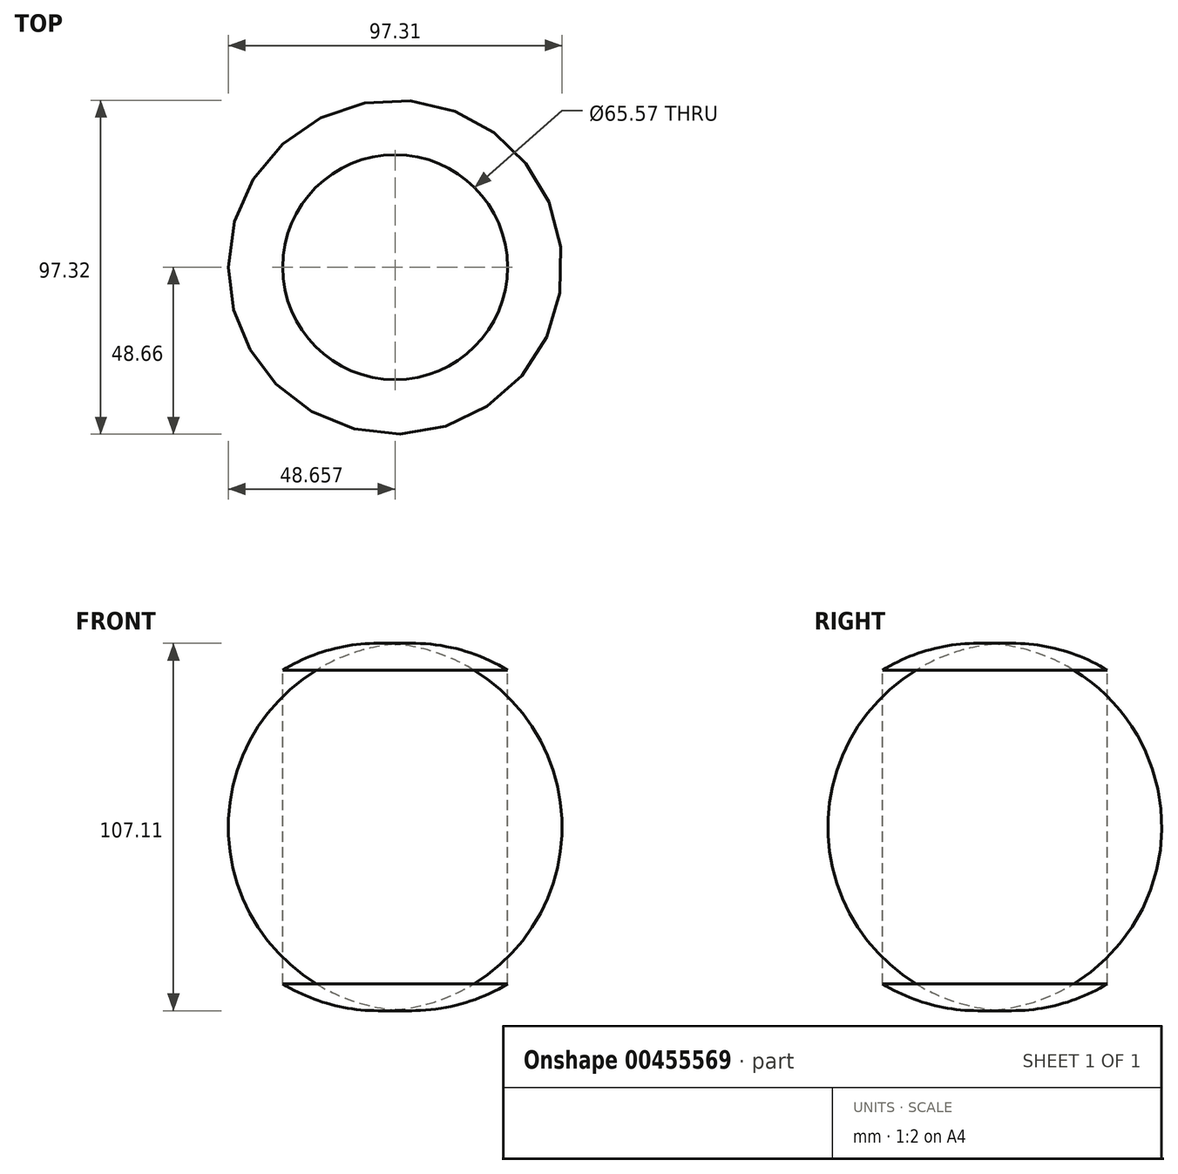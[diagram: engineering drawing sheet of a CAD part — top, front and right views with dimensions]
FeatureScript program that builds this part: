
annotation { "Feature Type Name" : "Feature", "Feature Type Description" : "" }
export const myFeature = defineFeature(function(context is Context, id is Id, definition is map)
    precondition{}
    {
        {
            var Q0;
            Q0=qCreatedBy(makeId("Top.planeOp"),FACE);
            var sketch = newSketch(context, id + "F0", { "sketchPlane" : qUnion([Q0])});
            skLineSegment(sketch, "E0", {"start": v(-39.7, 55.95) * mm, "end": v(-39.7, -36.1) * mm});
            skLineSegment(sketch, "E1", {"start": v(-13.54, 56.25) * mm, "end": v(-13.54, -35.8) * mm});
            skArc(sketch, "E2", {"start": v(-13.54, -35.8) * mm, "mid": v(33.96, 10.23) * mm, "end": v(-13.54, 56.25) * mm});
            skSolve(sketch);
        }
        {
            var Q0;
            Q0=makeQuery(id+"F0.imprint","IMPRINT",FACE,{"disambiguationData":[TD([[makeQuery(id+"F0.imprint","IMPRINT",EDGE,{"derivedFrom":sQuery(id+"F0.wireOp",EDGE,"E1")}),1.0]])]});
            var Q1;
            Q1=sQuery(id+"F0.wireOp",EDGE,"E0");
            revolve(context, id + "F1", {"entities" : qUnion([Q0]), "axis" : qUnion([Q1]), "revolveType" : RevolveType.FULL});
        }
        {
            var Q0;
            Q0=makeQuery(id+"F1.opRevolve","SWEPT_BODY",BODY,{"disambiguationData":[OSD([sQuery(id+"F0.wireOp",EDGE,"E1"),sQuery(id+"F0.wireOp",EDGE,"E2")])]});
            var Q1;
            Q1=qCreatedBy(makeId("Right.planeOp"),FACE);
            mirror(context, id + "F2", {"operationType" : NewBodyOperationType.ADD, "entities" : qUnion([Q0]), "mirrorPlane" : qUnion([Q1])});
        }
        {
            var Q0;
            Q0=makeQuery(id+"F1.opRevolve","SWEPT_BODY",BODY,{"disambiguationData":[OSD([sQuery(id+"F0.wireOp",EDGE,"E1"),sQuery(id+"F0.wireOp",EDGE,"E2")])]});
            deleteBodies(context, id + "F3", {"entities" : qUnion([Q0])});
        }
        {
            var Q0;
            Q0=qCreatedBy(makeId("Front.planeOp"),FACE);
            var sketch = newSketch(context, id + "F4", { "sketchPlane" : qUnion([Q0])});
            skLineSegment(sketch, "E3", {"start": v(-43.01, 56.55) * mm, "end": v(-43.01, -34.9) * mm});
            skLineSegment(sketch, "E4", {"start": v(-10.23, 56.85) * mm, "end": v(-10.23, -34.6) * mm});
            skArc(sketch, "E5", {"start": v(-10.23, -34.6) * mm, "mid": v(15.44, 11.13) * mm, "end": v(-10.23, 56.85) * mm});
            skSolve(sketch);
        }
        {
            var Q0;
            Q0=makeQuery(id+"F4.imprint","IMPRINT",FACE,{"disambiguationData":[TD([[makeQuery(id+"F4.imprint","IMPRINT",EDGE,{"derivedFrom":sQuery(id+"F4.wireOp",EDGE,"E4")}),1.0]])]});
            var Q1;
            Q1=sQuery(id+"F4.wireOp",EDGE,"E3");
            revolve(context, id + "F5", {"entities" : qUnion([Q0]), "axis" : qUnion([Q1]), "revolveType" : RevolveType.FULL});
        }
        {
            var Q0;
            Q0=makeQuery(id+"F5.opRevolve","SWEPT_BODY",BODY,{"disambiguationData":[OSD([sQuery(id+"F4.wireOp",EDGE,"E4"),sQuery(id+"F4.wireOp",EDGE,"E5")])]});
            var Q1;
            Q1=qCreatedBy(makeId("Front.planeOp"),FACE);
            mirror(context, id + "F6", {"operationType" : NewBodyOperationType.ADD, "entities" : qUnion([Q0]), "mirrorPlane" : qUnion([Q1])});
        }
        {
            var Q0;
            Q0=makeQuery(id+"F5.opRevolve","SWEPT_BODY",BODY,{"disambiguationData":[OSD([sQuery(id+"F4.wireOp",EDGE,"E4"),sQuery(id+"F4.wireOp",EDGE,"E5")])]});
            var Q1;
            Q1=qCreatedBy(makeId("Front.planeOp"),FACE);
            mirror(context, id + "F7", {"operationType" : NewBodyOperationType.ADD, "entities" : qUnion([Q0]), "mirrorPlane" : qUnion([Q1])});
        }
    });
